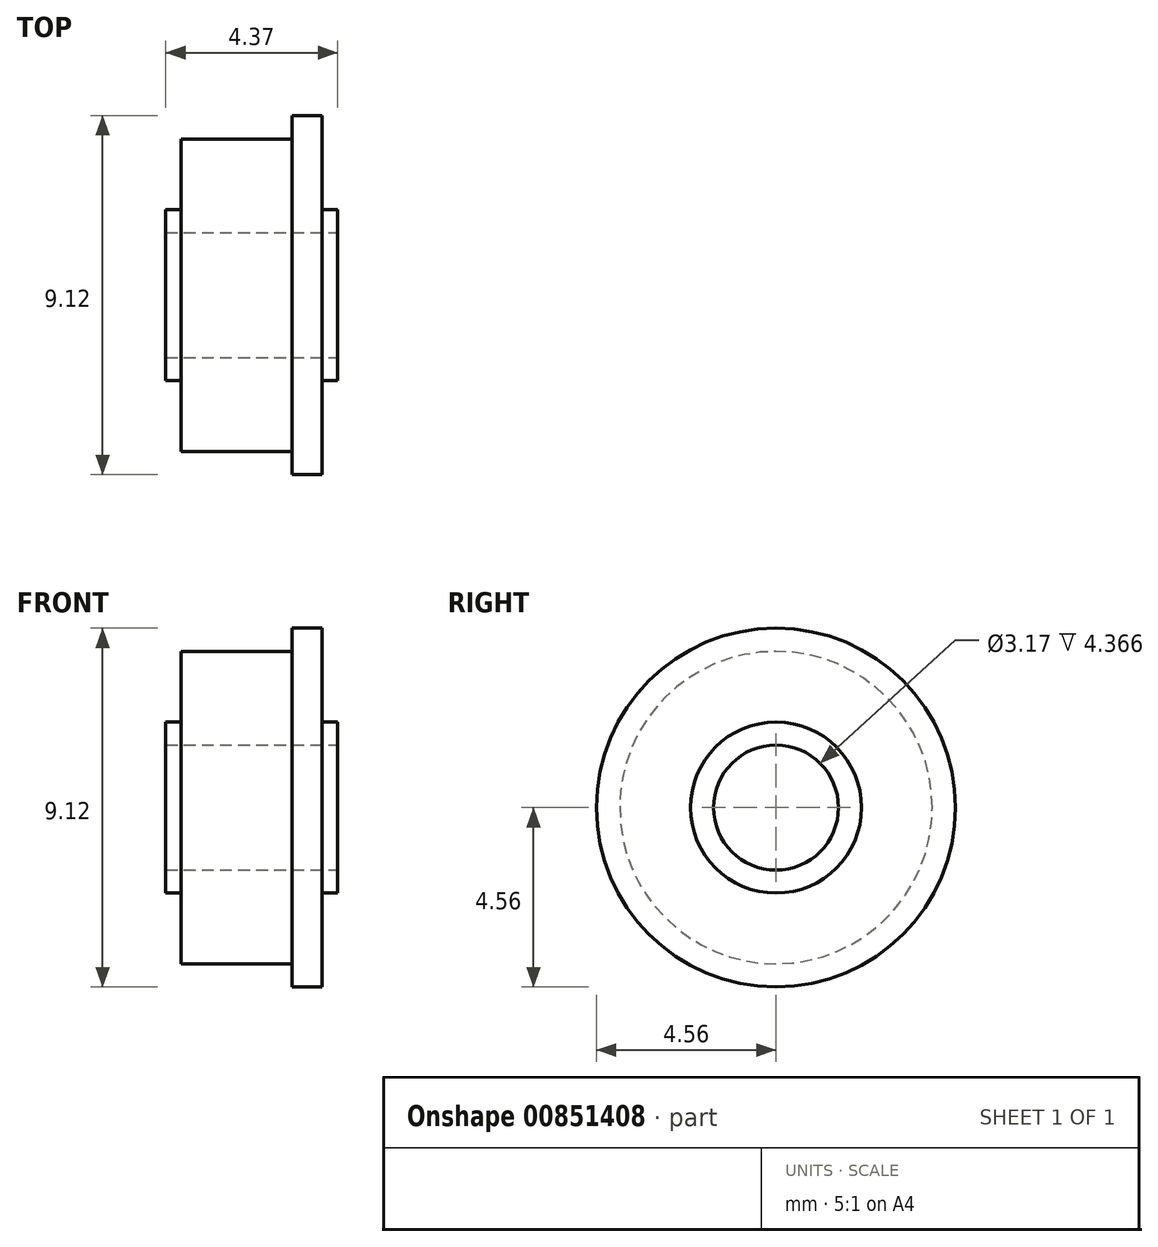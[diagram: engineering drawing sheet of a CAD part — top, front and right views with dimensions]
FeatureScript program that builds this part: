
annotation { "Feature Type Name" : "Feature", "Feature Type Description" : "" }
export const myFeature = defineFeature(function(context is Context, id is Id, definition is map)
    precondition{}
    {
        {
            var Q0;
            Q0=qCreatedBy(makeId("Front.planeOp"),FACE);
            var sketch = newSketch(context, id + "F0", { "sketchPlane" : qUnion([Q0])});
            skLineSegment(sketch, "E0", {"start": v(0, 1.59) * mm, "end": v(0, 2.17) * mm});
            skLineSegment(sketch, "E1", {"start": v(0, 2.17) * mm, "end": v(0.4, 2.17) * mm});
            skLineSegment(sketch, "E2", {"start": v(0.4, 2.17) * mm, "end": v(0.4, 3.97) * mm});
            skLineSegment(sketch, "E3", {"start": v(0.4, 3.97) * mm, "end": v(3.2, 3.97) * mm});
            skLineSegment(sketch, "E4", {"start": v(3.2, 3.97) * mm, "end": v(3.2, 4.56) * mm});
            skLineSegment(sketch, "E5", {"start": v(3.2, 4.56) * mm, "end": v(3.97, 4.56) * mm});
            skLineSegment(sketch, "E6", {"start": v(3.97, 4.56) * mm, "end": v(3.97, 2.17) * mm});
            skLineSegment(sketch, "E7", {"start": v(3.97, 2.17) * mm, "end": v(4.37, 2.17) * mm});
            skLineSegment(sketch, "E8", {"start": v(4.37, 2.17) * mm, "end": v(4.37, 1.59) * mm});
            skLineSegment(sketch, "E9", {"start": v(4.37, 1.59) * mm, "end": v(0, 1.59) * mm});
            skLineSegment(sketch, "E10", {"start": v(0, 0) * mm, "end": v(-9.15, 0) * mm, "construction": true});
            skSolve(sketch);
        }
        {
            var Q0;
            Q0 = qSketchRegion(id + "F0", true);
            var Q1;
            Q1=sQuery(id+"F0.wireOp",EDGE,"E10");
            revolve(context, id + "F1", {"surfaceOperationType" : NewSurfaceOperationType.NEW, "entities" : qUnion([Q0]), "axis" : qUnion([Q1]), "revolveType" : RevolveType.FULL});
        }
    });
